# Revit family: 1880100SR
name_source: partatom
category: Pipe Accessories
units: mm (PartAtom-declared; Revit-internal decimal feet)

## family parameters
Always vertical = Yes
Cut with Voids When Loaded = Yes
OmniClass Number = 23.45.00.00
OmniClass Title = Sanitary, Laundry, and Cleaning Equipment
Part Type = Valve - Breaks Into
Round Connector Dimension = Use Diameter
Shared = No
Work Plane-Based = No

## types (1)
- 1880100SR
    A = 204 mm  [stored 0.669291 ft]
    B = 153 mm
    C = 89 mm  [stored 0.291995 ft]
    Compatible Fluids = water; water + glycol 50% max
    D = 74 mm
    Description = Magnetic dirt separator I-MAG XL
    E = 129 mm
    F = 97 mm  [stored 0.318241 ft]
    G = 25 mm  [stored 0.082021 ft]
    ITAP_Body_material_Silver = ITAP Body Material_Silver
    ITAP_body_material = ITAP Body Material_Black
    ITAP_valve_material = ITAP Body Material_Golden
    KV = 6.3 m3/h
    Manufacturer = ITAP S.p.A.
    Max Pressure = 3 bar
    Stainless Steel cartridge filteration rating = 500 μm (pre-installed) - 800 μm (supplied in package)
    Temparature = 0 - 90°C
    URL = https://www.itap.it

note: [stored X ft] marks values corroborated as IEEE doubles in the binary element streams (Revit-internal decimal feet)
